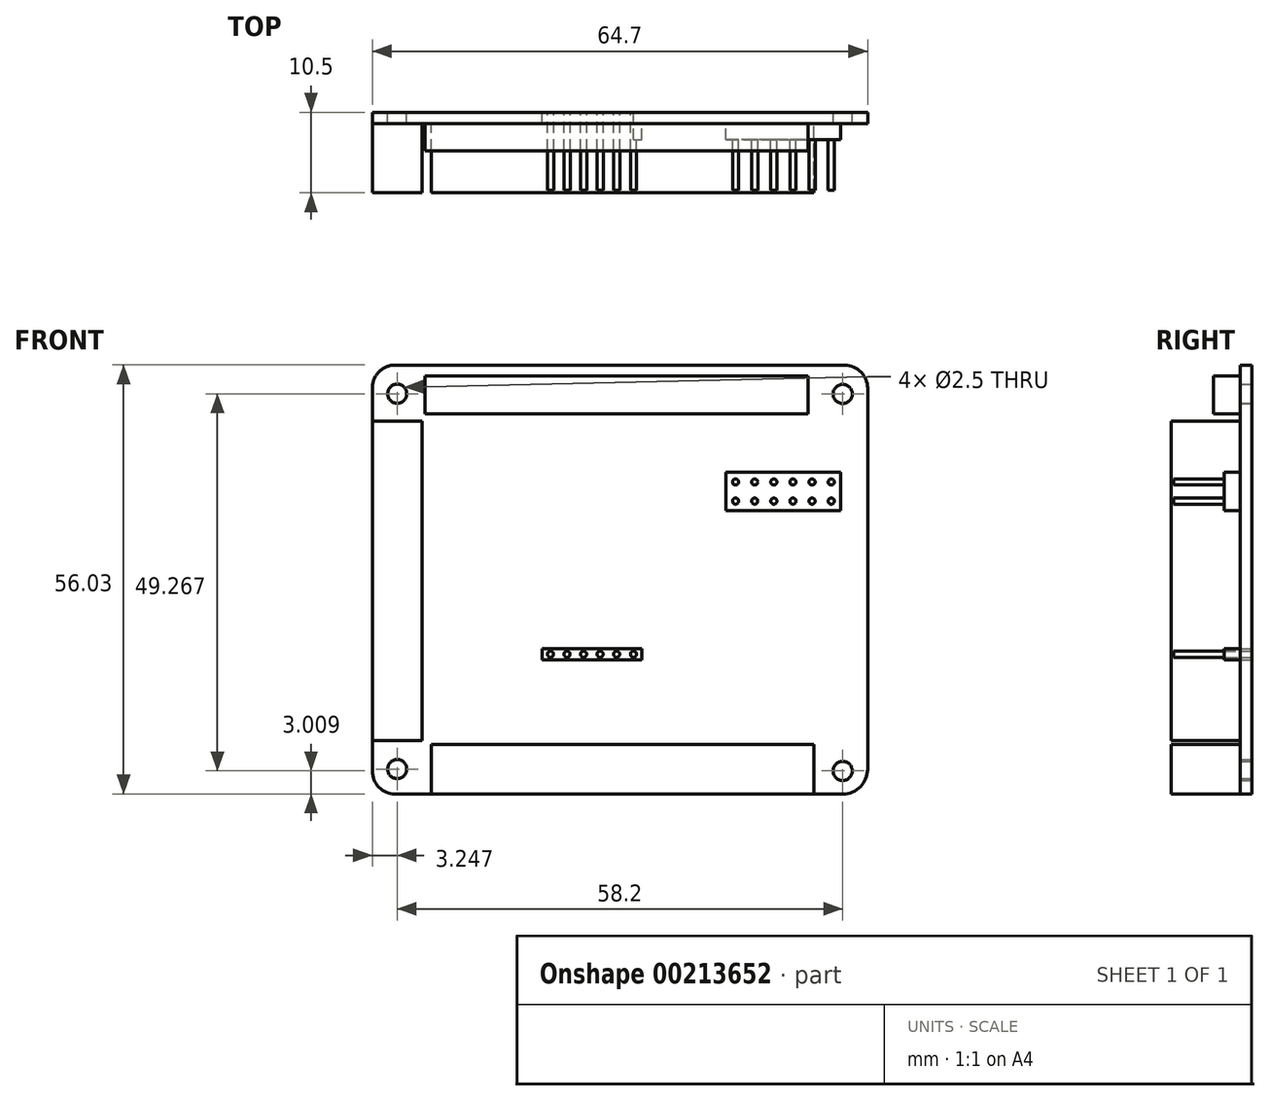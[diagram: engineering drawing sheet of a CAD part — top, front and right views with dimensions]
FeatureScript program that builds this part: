
annotation { "Feature Type Name" : "Feature", "Feature Type Description" : "" }
export const myFeature = defineFeature(function(context is Context, id is Id, definition is map)
    precondition{}
    {
        {
            var Q0;
            Q0=qCreatedBy(makeId("Front.planeOp"),FACE);
            var sketch = newSketch(context, id + "F0", { "sketchPlane" : qUnion([Q0])});
            skLineSegment(sketch, "E0", {"start": v(38.73, 25.6) * mm, "end": v(38.73, -24.14) * mm});
            skLineSegment(sketch, "E1", {"start": v(35.48, -27.4) * mm, "end": v(-22.97, -27.4) * mm});
            skLineSegment(sketch, "E2", {"start": v(-25.97, 8.8) * mm, "end": v(-25.97, 25.64) * mm});
            skLineSegment(sketch, "E3", {"start": v(35.73, 28.6) * mm, "end": v(-22.97, 28.64) * mm});
            skLineSegment(sketch, "E4", {"start": v(38.73, 28.6) * mm, "end": v(38.73, 24.86) * mm, "construction": true});
            skPoint(sketch, "E5.visualSharp", {"position": v(-25.97, 28.64) * mm});
            skArc(sketch, "E5.filletArc", {"start": v(-22.97, 28.64) * mm, "mid": v(-25.1, 27.76) * mm, "end": v(-25.97, 25.64) * mm});
            skPoint(sketch, "E6.visualSharp", {"position": v(-25.97, -27.4) * mm});
            skArc(sketch, "E6.filletArc", {"start": v(-25.97, -24.4) * mm, "mid": v(-25.1, -26.51) * mm, "end": v(-22.97, -27.4) * mm});
            skPoint(sketch, "E7.visualSharp", {"position": v(38.73, -27.4) * mm});
            skArc(sketch, "E7.filletArc", {"start": v(35.48, -27.4) * mm, "mid": v(37.77, -26.44) * mm, "end": v(38.73, -24.14) * mm});
            skPoint(sketch, "E8.visualSharp", {"position": v(38.73, 28.6) * mm});
            skArc(sketch, "E8.filletArc", {"start": v(38.73, 25.6) * mm, "mid": v(37.85, 27.73) * mm, "end": v(35.73, 28.6) * mm});
            skLineSegment(sketch, "E9", {"start": v(38.73, 24.86) * mm, "end": v(35.48, 24.86) * mm});
            skCircle(sketch, "E10", {"center": v(35.48, 24.86) * mm, "radius": 1.25 * mm});
            skLineSegment(sketch, "E11", {"start": v(38.73, -27.4) * mm, "end": v(38.73, -24.14) * mm, "construction": true});
            skLineSegment(sketch, "E12", {"start": v(35.48, 24.86) * mm, "end": v(35.48, -41.23) * mm, "construction": true});
            skLineSegment(sketch, "E13", {"start": v(38.73, -24.14) * mm, "end": v(35.48, -24.14) * mm, "construction": true});
            skLineSegment(sketch, "E14", {"start": v(-25.97, -27.4) * mm, "end": v(-22.72, -27.4) * mm, "construction": true});
            skLineSegment(sketch, "E15", {"start": v(-15.1, 28.63) * mm, "end": v(-15.1, 22.23) * mm, "construction": true});
            skLineSegment(sketch, "E16", {"start": v(-25.97, 22.23) * mm, "end": v(-19.07, 22.23) * mm, "construction": true});
            skLineSegment(sketch, "E17", {"start": v(-19.07, 22.23) * mm, "end": v(-19.07, 27.23) * mm});
            skLineSegment(sketch, "E18", {"start": v(-19.07, 22.23) * mm, "end": v(30.93, 22.23) * mm});
            skLineSegment(sketch, "E19", {"start": v(30.93, 22.23) * mm, "end": v(30.93, 27.23) * mm});
            skLineSegment(sketch, "E20", {"start": v(-19.07, 27.23) * mm, "end": v(30.93, 27.23) * mm});
            skCircle(sketch, "E21", {"center": v(35.48, -24.38) * mm, "radius": 1.25 * mm});
            skCircle(sketch, "E22", {"center": v(-22.72, -24.14) * mm, "radius": 1.25 * mm});
            skLineSegment(sketch, "E23", {"start": v(-22.97, 28.64) * mm, "end": v(-22.97, 24.89) * mm, "construction": true});
            skLineSegment(sketch, "E24", {"start": v(-22.72, -27.4) * mm, "end": v(-22.72, 31.65) * mm, "construction": true});
            skLineSegment(sketch, "E25", {"start": v(-22.97, 24.89) * mm, "end": v(-22.09, 24.89) * mm, "construction": true});
            skCircle(sketch, "E26", {"center": v(-22.72, 24.89) * mm, "radius": 1.25 * mm});
            skLineSegment(sketch, "E27", {"start": v(-19.1, -27.4) * mm, "end": v(-19.1, -28.1) * mm, "construction": true});
            skLineSegment(sketch, "E28", {"start": v(-25.97, -24.4) * mm, "end": v(-25.97, 8.8) * mm});
            skPoint(sketch, "E29.endSnap0", {"position": v(37.1, -24.14) * mm});
            skLineSegment(sketch, "E30", {"start": v(38.73, -24.14) * mm, "end": v(31.73, -24.14) * mm, "construction": true});
            skLineSegment(sketch, "E31", {"start": v(31.73, -27.4) * mm, "end": v(31.73, -20.9) * mm});
            skLineSegment(sketch, "E32", {"start": v(31.73, -20.9) * mm, "end": v(-18.27, -20.9) * mm});
            skLineSegment(sketch, "E33", {"start": v(-18.27, -20.9) * mm, "end": v(-18.27, -27.4) * mm});
            skLineSegment(sketch, "E34", {"start": v(-22.97, -27.4) * mm, "end": v(-22.97, -20.4) * mm, "construction": true});
            skLineSegment(sketch, "E35", {"start": v(-25.97, -20.4) * mm, "end": v(-19.47, -20.4) * mm});
            skLineSegment(sketch, "E36", {"start": v(-19.47, -20.4) * mm, "end": v(-19.47, 21.3) * mm});
            skLineSegment(sketch, "E37", {"start": v(-19.47, 21.3) * mm, "end": v(-25.97, 21.3) * mm});
            skLineSegment(sketch, "E38", {"start": v(-3.77, -27.4) * mm, "end": v(-3.77, -8.4) * mm, "construction": true});
            skLineSegment(sketch, "E39", {"start": v(-3.77, -8.4) * mm, "end": v(38.73, -8.4) * mm, "construction": true});
            skLineSegment(sketch, "E40", {"start": v(-3.77, -8.4) * mm, "end": v(9.23, -8.4) * mm});
            skLineSegment(sketch, "E41", {"start": v(9.23, -8.4) * mm, "end": v(9.23, -9.9) * mm});
            skLineSegment(sketch, "E42", {"start": v(9.23, -9.9) * mm, "end": v(-3.77, -9.9) * mm});
            skLineSegment(sketch, "E43", {"start": v(-3.77, -9.9) * mm, "end": v(-3.77, -8.4) * mm});
            skLineSegment(sketch, "E44", {"start": v(-3.77, -9.9) * mm, "end": v(-1.61, -9.9) * mm, "construction": true});
            skLineSegment(sketch, "E45", {"start": v(-1.61, -9.9) * mm, "end": v(-1.61, -8.4) * mm, "construction": true});
            skLineSegment(sketch, "E46", {"start": v(-1.61, -9.9) * mm, "end": v(0.55, -9.9) * mm});
            skLineSegment(sketch, "E47", {"start": v(0.55, -9.9) * mm, "end": v(0.55, -8.4) * mm, "construction": true});
            skLineSegment(sketch, "E48", {"start": v(0.55, -9.9) * mm, "end": v(2.7, -9.9) * mm});
            skLineSegment(sketch, "E49", {"start": v(2.7, -9.9) * mm, "end": v(2.7, -8.4) * mm, "construction": true});
            skLineSegment(sketch, "E50", {"start": v(2.7, -9.9) * mm, "end": v(4.87, -9.9) * mm});
            skLineSegment(sketch, "E51", {"start": v(4.87, -9.9) * mm, "end": v(4.87, -8.4) * mm, "construction": true});
            skLineSegment(sketch, "E52", {"start": v(4.87, -9.9) * mm, "end": v(7.03, -9.9) * mm});
            skLineSegment(sketch, "E53", {"start": v(7.03, -9.9) * mm, "end": v(7.03, -8.4) * mm, "construction": true});
            skLineSegment(sketch, "E54", {"start": v(-2.7, -8.4) * mm, "end": v(-2.7, -9.9) * mm, "construction": true});
            skPoint(sketch, "E54.startSnap0", {"position": v(-2.7, -9.9) * mm});
            skLineSegment(sketch, "E55", {"start": v(-0.53, -9.9) * mm, "end": v(-0.53, -8.4) * mm, "construction": true});
            skLineSegment(sketch, "E56", {"start": v(1.63, -9.9) * mm, "end": v(1.63, -8.4) * mm, "construction": true});
            skLineSegment(sketch, "E57", {"start": v(3.79, -9.9) * mm, "end": v(3.79, -8.4) * mm, "construction": true});
            skLineSegment(sketch, "E58", {"start": v(5.95, -9.9) * mm, "end": v(5.95, -8.4) * mm, "construction": true});
            skCircle(sketch, "E59", {"center": v(-2.7, -9.14) * mm, "radius": 0.4 * mm});
            skCircle(sketch, "E60", {"center": v(-0.53, -9.14) * mm, "radius": 0.4 * mm});
            skCircle(sketch, "E61", {"center": v(1.63, -9.14) * mm, "radius": 0.4 * mm});
            skCircle(sketch, "E62", {"center": v(3.79, -9.14) * mm, "radius": 0.4 * mm});
            skCircle(sketch, "E63", {"center": v(5.95, -9.14) * mm, "radius": 0.4 * mm});
            skLineSegment(sketch, "E64", {"start": v(9.23, -8.4) * mm, "end": v(8.15, -8.4) * mm});
            skLineSegment(sketch, "E65", {"start": v(8.15, -8.4) * mm, "end": v(8.15, -9.9) * mm});
            skCircle(sketch, "E66", {"center": v(8.15, -9.14) * mm, "radius": 0.4 * mm});
            skLineSegment(sketch, "E67", {"start": v(33.11, 28.6) * mm, "end": v(33.1, 9.6) * mm, "construction": true});
            skLineSegment(sketch, "E68", {"start": v(38.73, 9.6) * mm, "end": v(20.23, 9.6) * mm, "construction": true});
            skLineSegment(sketch, "E69", {"start": v(20.23, 9.6) * mm, "end": v(20.23, 14.6) * mm});
            skLineSegment(sketch, "E70", {"start": v(20.23, 14.6) * mm, "end": v(35.23, 14.6) * mm});
            skLineSegment(sketch, "E71", {"start": v(35.23, 14.6) * mm, "end": v(35.23, 9.6) * mm});
            skLineSegment(sketch, "E72", {"start": v(35.23, 9.6) * mm, "end": v(20.23, 9.6) * mm});
            skLineSegment(sketch, "E73", {"start": v(20.23, 12.1) * mm, "end": v(35.23, 12.1) * mm, "construction": true});
            skLineSegment(sketch, "E74", {"start": v(20.23, 12.1) * mm, "end": v(22.73, 12.1) * mm, "construction": true});
            skLineSegment(sketch, "E75", {"start": v(22.73, 12.1) * mm, "end": v(22.73, 14.6) * mm, "construction": true});
            skLineSegment(sketch, "E76", {"start": v(22.73, 12.1) * mm, "end": v(25.23, 12.1) * mm, "construction": true});
            skLineSegment(sketch, "E77", {"start": v(25.23, 12.1) * mm, "end": v(25.23, 14.6) * mm, "construction": true});
            skLineSegment(sketch, "E78", {"start": v(25.23, 12.1) * mm, "end": v(27.73, 12.1) * mm, "construction": true});
            skLineSegment(sketch, "E79", {"start": v(27.73, 12.1) * mm, "end": v(27.73, 14.6) * mm, "construction": true});
            skLineSegment(sketch, "E80", {"start": v(27.73, 12.1) * mm, "end": v(30.23, 12.1) * mm, "construction": true});
            skLineSegment(sketch, "E81", {"start": v(30.23, 12.1) * mm, "end": v(30.23, 14.6) * mm, "construction": true});
            skLineSegment(sketch, "E82", {"start": v(30.23, 12.1) * mm, "end": v(32.73, 12.1) * mm, "construction": true});
            skLineSegment(sketch, "E83", {"start": v(32.73, 12.1) * mm, "end": v(32.73, 14.6) * mm, "construction": true});
            skLineSegment(sketch, "E84", {"start": v(22.73, 12.1) * mm, "end": v(22.73, 9.6) * mm, "construction": true});
            skLineSegment(sketch, "E85", {"start": v(25.23, 12.1) * mm, "end": v(25.23, 9.6) * mm, "construction": true});
            skLineSegment(sketch, "E86", {"start": v(27.73, 12.1) * mm, "end": v(27.73, 9.6) * mm, "construction": true});
            skLineSegment(sketch, "E87", {"start": v(30.23, 12.1) * mm, "end": v(30.23, 9.6) * mm, "construction": true});
            skLineSegment(sketch, "E88", {"start": v(32.73, 12.1) * mm, "end": v(32.73, 9.6) * mm, "construction": true});
            skLineSegment(sketch, "E89", {"start": v(21.48, 12.1) * mm, "end": v(21.48, 14.6) * mm, "construction": true});
            skLineSegment(sketch, "E90", {"start": v(23.98, 12.1) * mm, "end": v(23.98, 14.6) * mm, "construction": true});
            skLineSegment(sketch, "E91", {"start": v(26.48, 12.1) * mm, "end": v(26.48, 14.6) * mm, "construction": true});
            skLineSegment(sketch, "E92", {"start": v(28.98, 12.1) * mm, "end": v(28.98, 14.6) * mm, "construction": true});
            skLineSegment(sketch, "E93", {"start": v(31.48, 12.1) * mm, "end": v(31.48, 14.6) * mm, "construction": true});
            skLineSegment(sketch, "E94", {"start": v(21.48, 12.1) * mm, "end": v(21.48, 9.6) * mm, "construction": true});
            skLineSegment(sketch, "E95", {"start": v(23.98, 12.1) * mm, "end": v(23.98, 9.6) * mm, "construction": true});
            skLineSegment(sketch, "E96", {"start": v(26.48, 12.1) * mm, "end": v(26.48, 9.6) * mm, "construction": true});
            skLineSegment(sketch, "E97", {"start": v(28.98, 12.1) * mm, "end": v(28.98, 9.6) * mm, "construction": true});
            skLineSegment(sketch, "E98", {"start": v(31.48, 12.1) * mm, "end": v(31.48, 9.6) * mm, "construction": true});
            skCircle(sketch, "E99", {"center": v(21.48, 10.86) * mm, "radius": 0.4 * mm});
            skCircle(sketch, "E100", {"center": v(23.98, 10.86) * mm, "radius": 0.4 * mm});
            skCircle(sketch, "E101", {"center": v(26.48, 10.86) * mm, "radius": 0.4 * mm});
            skCircle(sketch, "E102", {"center": v(28.98, 10.86) * mm, "radius": 0.4 * mm});
            skCircle(sketch, "E103", {"center": v(31.48, 10.86) * mm, "radius": 0.4 * mm});
            skCircle(sketch, "E104", {"center": v(21.48, 13.36) * mm, "radius": 0.4 * mm});
            skCircle(sketch, "E105", {"center": v(23.98, 13.36) * mm, "radius": 0.4 * mm});
            skCircle(sketch, "E106", {"center": v(26.48, 13.36) * mm, "radius": 0.4 * mm});
            skCircle(sketch, "E107", {"center": v(28.98, 13.36) * mm, "radius": 0.4 * mm});
            skCircle(sketch, "E108", {"center": v(31.48, 13.36) * mm, "radius": 0.4 * mm});
            skLineSegment(sketch, "E109", {"start": v(32.73, 12.1) * mm, "end": v(33.98, 12.1) * mm, "construction": true});
            skLineSegment(sketch, "E110", {"start": v(33.98, 12.1) * mm, "end": v(33.98, 14.6) * mm, "construction": true});
            skLineSegment(sketch, "E111", {"start": v(33.98, 12.1) * mm, "end": v(33.98, 9.6) * mm, "construction": true});
            skCircle(sketch, "E112", {"center": v(33.98, 10.86) * mm, "radius": 0.4 * mm});
            skCircle(sketch, "E113", {"center": v(33.98, 13.36) * mm, "radius": 0.4 * mm});
            skSolve(sketch);
        }
        {
            var Q0;
            Q0=makeQuery(id+"F0.imprint","IMPRINT",FACE,{"disambiguationData":[TD([[makeQuery(id+"F0.imprint","IMPRINT",EDGE,{"derivedFrom":sQuery(id+"F0.wireOp",EDGE,"E3")}),1.0]])]});
            extrude(context, id + "F1", {"entities" : qUnion([Q0]), "depth" : 1.5 * mm});
        }
        {
            var Q0;
            {var subQ0=sQuery(id+"F0.wireOp",EDGE,"E35");Q0=makeQuery(id+"F0.imprint","IMPRINT",FACE,{"disambiguationData":[TD([[makeQuery(id+"F0.imprint","IMPRINT",EDGE,{"derivedFrom":subQ0}),1.0]])]});}
            var Q1;
            {var subQ0=sQuery(id+"F0.wireOp",EDGE,"E31");Q1=makeQuery(id+"F0.imprint","IMPRINT",FACE,{"disambiguationData":[TD([[makeQuery(id+"F0.imprint","IMPRINT",EDGE,{"derivedFrom":subQ0}),1.0]])]});}
            extrude(context, id + "F2", {"entities" : qUnion([Q0, Q1]), "operationType" : NewBodyOperationType.ADD, "depth" : 10.5 * mm});
        }
        {
            var Q0;
            {var subQ5=sQuery(id+"F0.wireOp",EDGE,"E40");Q0=makeQuery(id+"F0.imprint","IMPRINT",FACE,{"disambiguationData":[TD([[makeQuery(id+"F0.imprint","IMPRINT",EDGE,{"derivedFrom":subQ5}),-1.0]])]});}
            var Q1;
            {var subQ6=sQuery(id+"F0.wireOp",EDGE,"E41");Q1=makeQuery(id+"F0.imprint","IMPRINT",FACE,{"disambiguationData":[TD([[makeQuery(id+"F0.imprint","IMPRINT",EDGE,{"derivedFrom":subQ6}),-1.0]])]});}
            var Q2;
            Q2=makeQuery(id+"F0.imprint","IMPRINT",FACE,{"disambiguationData":[TD([[makeQuery(id+"F0.imprint","IMPRINT",EDGE,{"derivedFrom":sQuery(id+"F0.wireOp",EDGE,"E69")}),-1.0]])]});
            extrude(context, id + "F3", {"entities" : qUnion([Q0, Q1, Q2]), "operationType" : NewBodyOperationType.ADD, "depth" : 3.6 * mm});
        }
        {
            var Q0;
            Q0=makeQuery(id+"F0.imprint","IMPRINT",FACE,{"disambiguationData":[TD([[makeQuery(id+"F0.imprint","IMPRINT",EDGE,{"derivedFrom":sQuery(id+"F0.wireOp",EDGE,"E104")}),1.0]])]});
            var Q1;
            Q1=makeQuery(id+"F0.imprint","IMPRINT",FACE,{"disambiguationData":[TD([[makeQuery(id+"F0.imprint","IMPRINT",EDGE,{"derivedFrom":sQuery(id+"F0.wireOp",EDGE,"E105")}),1.0]])]});
            var Q2;
            Q2=makeQuery(id+"F0.imprint","IMPRINT",FACE,{"disambiguationData":[TD([[makeQuery(id+"F0.imprint","IMPRINT",EDGE,{"derivedFrom":sQuery(id+"F0.wireOp",EDGE,"E106")}),1.0]])]});
            var Q3;
            Q3=makeQuery(id+"F0.imprint","IMPRINT",FACE,{"disambiguationData":[TD([[makeQuery(id+"F0.imprint","IMPRINT",EDGE,{"derivedFrom":sQuery(id+"F0.wireOp",EDGE,"E107")}),1.0]])]});
            var Q4;
            Q4=makeQuery(id+"F0.imprint","IMPRINT",FACE,{"disambiguationData":[TD([[makeQuery(id+"F0.imprint","IMPRINT",EDGE,{"derivedFrom":sQuery(id+"F0.wireOp",EDGE,"E108")}),1.0]])]});
            var Q5;
            Q5=makeQuery(id+"F0.imprint","IMPRINT",FACE,{"disambiguationData":[TD([[makeQuery(id+"F0.imprint","IMPRINT",EDGE,{"derivedFrom":sQuery(id+"F0.wireOp",EDGE,"E113")}),1.0]])]});
            var Q6;
            Q6=makeQuery(id+"F0.imprint","IMPRINT",FACE,{"disambiguationData":[TD([[makeQuery(id+"F0.imprint","IMPRINT",EDGE,{"derivedFrom":sQuery(id+"F0.wireOp",EDGE,"E99")}),1.0]])]});
            var Q7;
            Q7=makeQuery(id+"F0.imprint","IMPRINT",FACE,{"disambiguationData":[TD([[makeQuery(id+"F0.imprint","IMPRINT",EDGE,{"derivedFrom":sQuery(id+"F0.wireOp",EDGE,"E100")}),1.0]])]});
            var Q8;
            Q8=makeQuery(id+"F0.imprint","IMPRINT",FACE,{"disambiguationData":[TD([[makeQuery(id+"F0.imprint","IMPRINT",EDGE,{"derivedFrom":sQuery(id+"F0.wireOp",EDGE,"E101")}),1.0]])]});
            var Q9;
            Q9=makeQuery(id+"F0.imprint","IMPRINT",FACE,{"disambiguationData":[TD([[makeQuery(id+"F0.imprint","IMPRINT",EDGE,{"derivedFrom":sQuery(id+"F0.wireOp",EDGE,"E102")}),1.0]])]});
            var Q10;
            Q10=makeQuery(id+"F0.imprint","IMPRINT",FACE,{"disambiguationData":[TD([[makeQuery(id+"F0.imprint","IMPRINT",EDGE,{"derivedFrom":sQuery(id+"F0.wireOp",EDGE,"E103")}),1.0]])]});
            var Q11;
            Q11=makeQuery(id+"F0.imprint","IMPRINT",FACE,{"disambiguationData":[TD([[makeQuery(id+"F0.imprint","IMPRINT",EDGE,{"derivedFrom":sQuery(id+"F0.wireOp",EDGE,"E112")}),1.0]])]});
            var Q12;
            Q12=makeQuery(id+"F0.imprint","IMPRINT",FACE,{"disambiguationData":[TD([[makeQuery(id+"F0.imprint","IMPRINT",EDGE,{"derivedFrom":sQuery(id+"F0.wireOp",EDGE,"E59")}),1.0]])]});
            var Q13;
            Q13=makeQuery(id+"F0.imprint","IMPRINT",FACE,{"disambiguationData":[TD([[makeQuery(id+"F0.imprint","IMPRINT",EDGE,{"derivedFrom":sQuery(id+"F0.wireOp",EDGE,"E60")}),1.0]])]});
            var Q14;
            Q14=makeQuery(id+"F0.imprint","IMPRINT",FACE,{"disambiguationData":[TD([[makeQuery(id+"F0.imprint","IMPRINT",EDGE,{"derivedFrom":sQuery(id+"F0.wireOp",EDGE,"E61")}),1.0]])]});
            var Q15;
            Q15=makeQuery(id+"F0.imprint","IMPRINT",FACE,{"disambiguationData":[TD([[makeQuery(id+"F0.imprint","IMPRINT",EDGE,{"derivedFrom":sQuery(id+"F0.wireOp",EDGE,"E62")}),1.0]])]});
            var Q16;
            Q16=makeQuery(id+"F0.imprint","IMPRINT",FACE,{"disambiguationData":[TD([[makeQuery(id+"F0.imprint","IMPRINT",EDGE,{"derivedFrom":sQuery(id+"F0.wireOp",EDGE,"E63")}),1.0]])]});
            var Q17;
            {var subQ0=sQuery(id+"F0.wireOp",EDGE,"E66");var subQ1=sQuery(id+"F0.wireOp",EDGE,"E65");var subQ2=makeQuery(id+"F0.imprint","INTERSECT",VERTEX,{"disambiguationData":[OD(0.0)],"derivedFrom":[subQ1,subQ0]});Q17=makeQuery(id+"F0.imprint","IMPRINT",FACE,{"disambiguationData":[TD([[makeQuery(id+"F0.imprint","IMPRINT",EDGE,{"disambiguationData":[TD([[subQ2,-1.0]])],"derivedFrom":subQ1}),1.0]])]});}
            var Q18;
            {var subQ0=sQuery(id+"F0.wireOp",EDGE,"E66");var subQ1=sQuery(id+"F0.wireOp",EDGE,"E65");var subQ2=makeQuery(id+"F0.imprint","INTERSECT",VERTEX,{"disambiguationData":[OD(0.0)],"derivedFrom":[subQ1,subQ0]});Q18=makeQuery(id+"F0.imprint","IMPRINT",FACE,{"disambiguationData":[TD([[makeQuery(id+"F0.imprint","IMPRINT",EDGE,{"disambiguationData":[TD([[subQ2,-1.0]])],"derivedFrom":subQ1}),-1.0]])]});}
            extrude(context, id + "F4", {"entities" : qUnion([Q0, Q1, Q2, Q3, Q4, Q5, Q6, Q7, Q8, Q9, Q10, Q11, Q12, Q13, Q14, Q15, Q16, Q17, Q18]), "operationType" : NewBodyOperationType.ADD, "depth" : 10.2 * mm});
        }
        {
            var Q0;
            Q0=makeQuery(id+"F0.imprint","IMPRINT",FACE,{"disambiguationData":[TD([[makeQuery(id+"F0.imprint","IMPRINT",EDGE,{"derivedFrom":sQuery(id+"F0.wireOp",EDGE,"E17")}),-1.0]])]});
            extrude(context, id + "F5", {"entities" : qUnion([Q0]), "operationType" : NewBodyOperationType.ADD, "depth" : 5 * mm});
        }
    });
